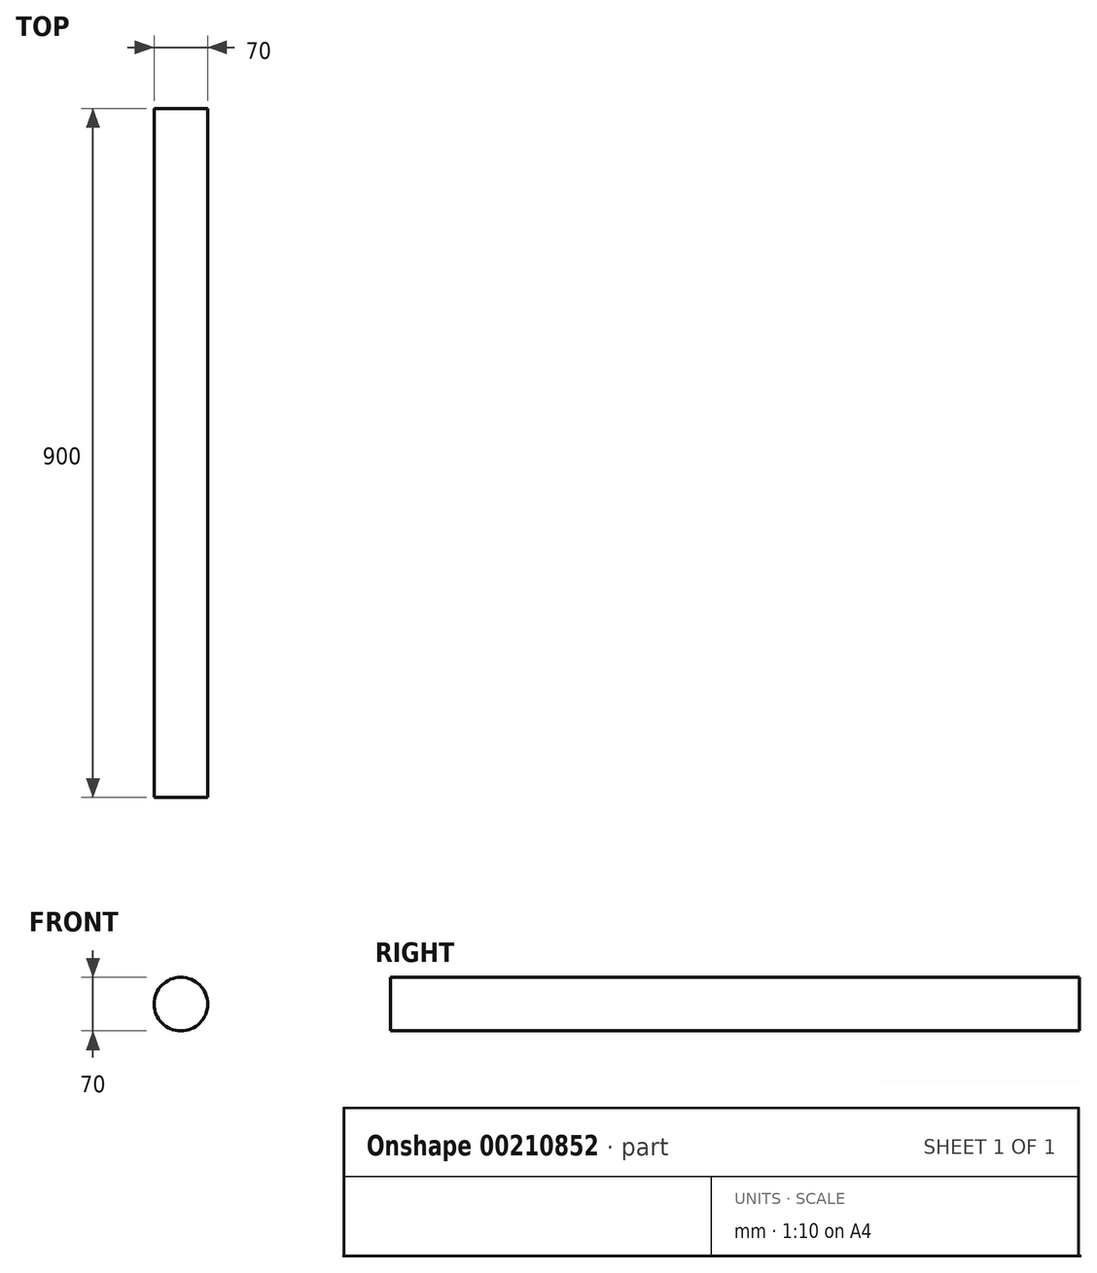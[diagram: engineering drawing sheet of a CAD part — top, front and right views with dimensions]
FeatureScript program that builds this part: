
annotation { "Feature Type Name" : "Feature", "Feature Type Description" : "" }
export const myFeature = defineFeature(function(context is Context, id is Id, definition is map)
    precondition{}
    {
        {
            var Q0;
            Q0=qCreatedBy(makeId("Front.planeOp"),FACE);
            var sketch = newSketch(context, id + "F0", { "sketchPlane" : qUnion([Q0])});
            skCircle(sketch, "E0", {"center": v(0, 0) * mm, "radius": 35 * mm});
            skSolve(sketch);
        }
        {
            var Q0;
            Q0=makeQuery(id+"F0.imprint","IMPRINT",FACE,{"disambiguationData":[TD([[makeQuery(id+"F0.imprint","IMPRINT",EDGE,{"derivedFrom":sQuery(id+"F0.wireOp",EDGE,"E0")}),1.0]])]});
            extrude(context, id + "F1", {"entities" : qUnion([Q0]), "depth" : 900 * mm});
        }
    });
